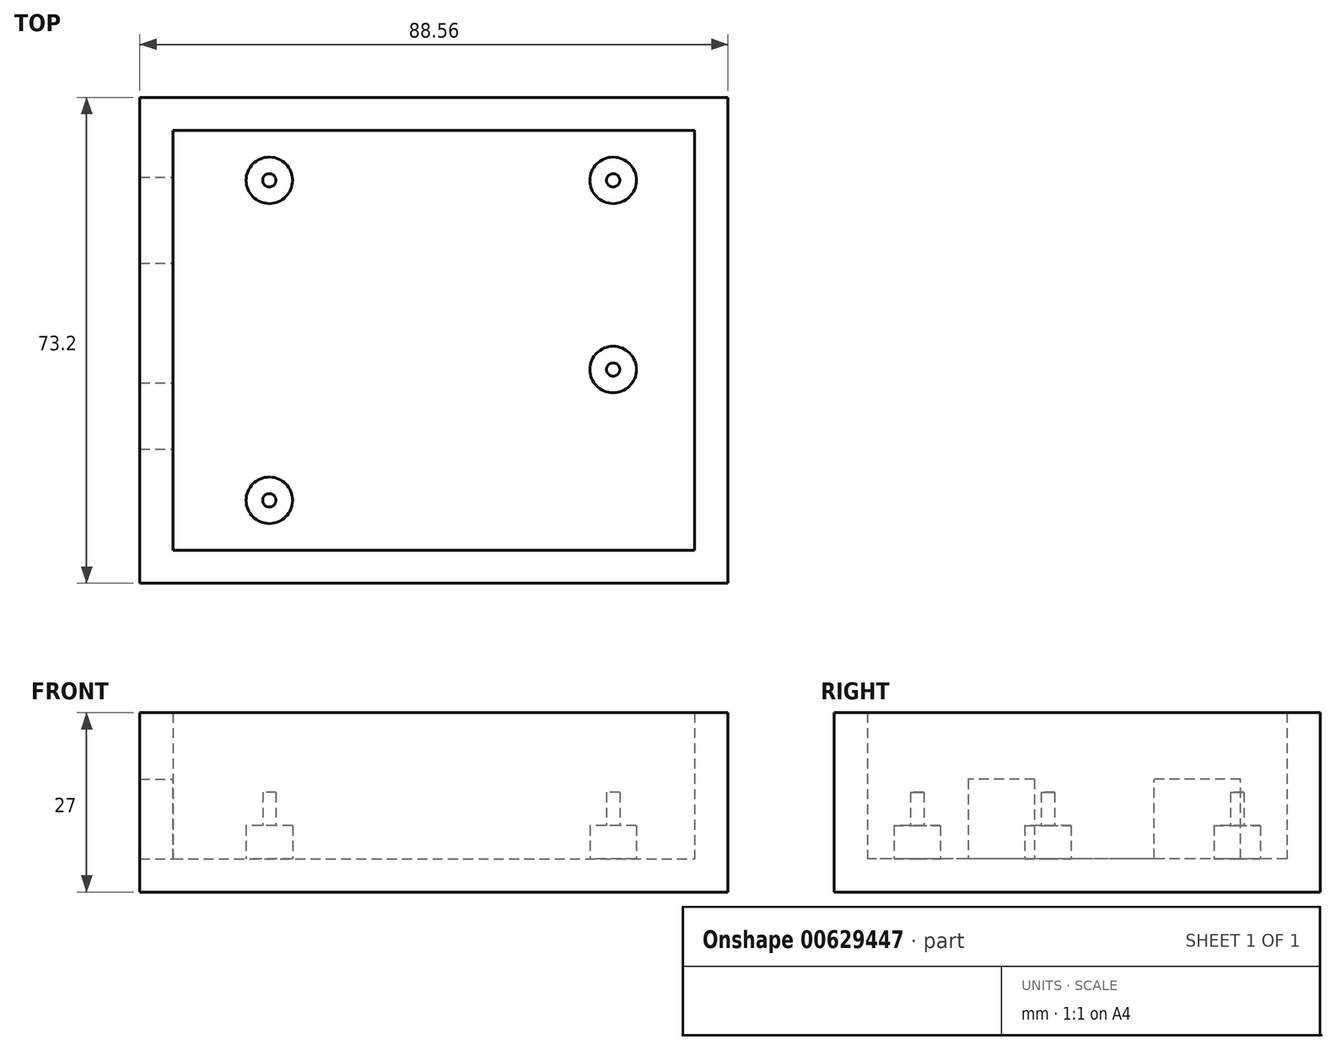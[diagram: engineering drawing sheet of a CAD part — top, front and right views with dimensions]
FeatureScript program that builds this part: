
annotation { "Feature Type Name" : "Feature", "Feature Type Description" : "" }
export const myFeature = defineFeature(function(context is Context, id is Id, definition is map)
    precondition{}
    {
        {
            var Q0;
            Q0=qCreatedBy(makeId("Top.planeOp"),FACE);
            var sketch = newSketch(context, id + "F0", { "sketchPlane" : qUnion([Q0])});
            skLineSegment(sketch, "E0.bottom", {"start": v(-32.7, 37.7) * mm, "end": v(33.07, 37.7) * mm});
            skLineSegment(sketch, "E0.top", {"start": v(-32.7, -15.5) * mm, "end": v(33.07, -15.5) * mm});
            skLineSegment(sketch, "E0.left", {"start": v(-32.7, 37.7) * mm, "end": v(-32.7, -15.5) * mm});
            skLineSegment(sketch, "E0.right", {"start": v(33.07, 37.7) * mm, "end": v(33.07, -15.5) * mm});
            skLineSegment(sketch, "E1.bottom", {"start": v(-39.2, 8.8) * mm, "end": v(-32.7, 8.8) * mm});
            skLineSegment(sketch, "E1.top", {"start": v(-39.2, -3.1) * mm, "end": v(-32.7, -3.1) * mm});
            skLineSegment(sketch, "E1.left", {"start": v(-39.2, 8.8) * mm, "end": v(-39.2, -3.1) * mm});
            skLineSegment(sketch, "E1.right", {"start": v(-32.7, 8.8) * mm, "end": v(-32.7, -3.1) * mm});
            skLineSegment(sketch, "E2.bottom", {"start": v(-36.41, 27.7) * mm, "end": v(-32.7, 27.7) * mm});
            skLineSegment(sketch, "E2.top", {"start": v(-36.41, 18.8) * mm, "end": v(-32.7, 18.8) * mm});
            skLineSegment(sketch, "E2.left", {"start": v(-36.41, 27.7) * mm, "end": v(-36.41, 18.8) * mm});
            skLineSegment(sketch, "E2.right", {"start": v(-32.7, 27.7) * mm, "end": v(-32.7, 18.8) * mm});
            skSolve(sketch);
        }
        {
            var Q0;
            Q0=qCreatedBy(makeId("Top.planeOp"),FACE);
            var sketch = newSketch(context, id + "F1", { "sketchPlane" : qUnion([Q0])});
            skLineSegment(sketch, "E3.bottom", {"start": v(-42.7, 47.7) * mm, "end": v(45.85, 47.7) * mm});
            skLineSegment(sketch, "E3.top", {"start": v(-42.7, -25.5) * mm, "end": v(45.85, -25.5) * mm});
            skLineSegment(sketch, "E3.left", {"start": v(-42.7, 47.7) * mm, "end": v(-42.7, -25.5) * mm});
            skLineSegment(sketch, "E3.right", {"start": v(45.85, 47.7) * mm, "end": v(45.85, -25.5) * mm});
            skLineSegment(sketch, "E4.direction1", {"start": v(-23.2, 35.2) * mm, "end": v(-23.2, -13) * mm, "construction": true});
            skSolve(sketch);
        }
        {
            var Q0;
            Q0=makeQuery(id+"F1.imprint","IMPRINT",FACE,{"disambiguationData":[TD([[makeQuery(id+"F1.imprint","IMPRINT",EDGE,{"derivedFrom":sQuery(id+"F1.wireOp",EDGE,"E3.bottom")}),-1.0]])]});
            extrude(context, id + "F2", {"entities" : qUnion([Q0]), "depth" : 22 * mm, "offsetDistance" : 25 * mm, "hasSecondDirection" : true, "secondDirectionOppositeDirection" : true, "secondDirectionDepth" : 5 * mm});
        }
        {
            var Q0;
            Q0=qCreatedBy(makeId("Top.planeOp"),FACE);
            var sketch = newSketch(context, id + "F3", { "sketchPlane" : qUnion([Q0])});
            skLineSegment(sketch, "E5.bottom", {"start": v(-37.7, 42.7) * mm, "end": v(40.85, 42.7) * mm});
            skLineSegment(sketch, "E5.top", {"start": v(-37.7, -20.5) * mm, "end": v(40.85, -20.5) * mm});
            skLineSegment(sketch, "E5.left", {"start": v(-37.7, 42.7) * mm, "end": v(-37.7, -20.5) * mm});
            skLineSegment(sketch, "E5.right", {"start": v(40.85, 42.7) * mm, "end": v(40.85, -20.5) * mm});
            skSolve(sketch);
        }
        {
            var Q0;
            Q0 = qSketchRegion(id + "F3", true);
            extrude(context, id + "F4", {"entities" : qUnion([Q0]), "operationType" : NewBodyOperationType.REMOVE, "depth" : 34.1 * mm, "offsetDistance" : 25 * mm});
        }
        {
            var Q0;
            Q0=qCreatedBy(makeId("Top.planeOp"),FACE);
            var sketch = newSketch(context, id + "F5", { "sketchPlane" : qUnion([Q0])});
            skLineSegment(sketch, "E6.bottom", {"start": v(-42.7, -25.5) * mm, "end": v(45.85, -25.5) * mm});
            skLineSegment(sketch, "E6.top", {"start": v(-42.7, 47.7) * mm, "end": v(45.85, 47.7) * mm});
            skLineSegment(sketch, "E6.left", {"start": v(-42.7, -25.5) * mm, "end": v(-42.7, 47.7) * mm});
            skLineSegment(sketch, "E6.right", {"start": v(45.85, -25.5) * mm, "end": v(45.85, 47.7) * mm});
            skSolve(sketch);
        }
        {
            var Q0;
            Q0=makeQuery(id+"F4.boolean.opBoolean","COPY",FACE,{"derivedFrom":makeQuery(id+"F4.opExtrude","SWEPT_FACE",FACE,{"disambiguationData":[OSD([sQuery(id+"F3.wireOp",EDGE,"E5.left")])]})});
            var sketch = newSketch(context, id + "F6", { "sketchPlane" : qUnion([Q0])});
            skLineSegment(sketch, "E7.bottom", {"start": v(35.7, 0) * mm, "end": v(22.7, 0) * mm});
            skLineSegment(sketch, "E7.top", {"start": v(35.7, 12) * mm, "end": v(22.7, 12) * mm});
            skLineSegment(sketch, "E7.left", {"start": v(35.7, 0) * mm, "end": v(35.7, 12) * mm});
            skLineSegment(sketch, "E7.right", {"start": v(22.7, 0) * mm, "end": v(22.7, 12) * mm});
            skLineSegment(sketch, "E8.bottom", {"start": v(4.7, 12) * mm, "end": v(-5.3, 12) * mm});
            skLineSegment(sketch, "E8.top", {"start": v(4.7, 0) * mm, "end": v(-5.3, 0) * mm});
            skLineSegment(sketch, "E8.left", {"start": v(4.7, 12) * mm, "end": v(4.7, 0) * mm});
            skLineSegment(sketch, "E8.right", {"start": v(-5.3, 12) * mm, "end": v(-5.3, 0) * mm});
            skSolve(sketch);
        }
        {
            var Q0;
            Q0=makeQuery(id+"F5.imprint","IMPRINT",FACE,{"disambiguationData":[TD([[makeQuery(id+"F5.imprint","IMPRINT",EDGE,{"derivedFrom":sQuery(id+"F5.wireOp",EDGE,"E6.bottom")}),1.0]])]});
            var sketch = newSketch(context, id + "F7", { "sketchPlane" : qUnion([Q0])});
            skCircle(sketch, "E9.0", {"center": v(28.57, 35.2) * mm, "radius": 3.5 * mm});
            skCircle(sketch, "E9.1", {"center": v(28.57, 6.7) * mm, "radius": 3.5 * mm});
            skCircle(sketch, "E9.2", {"center": v(-23.2, 35.2) * mm, "radius": 3.5 * mm});
            skCircle(sketch, "E9.3", {"center": v(-23.2, -13) * mm, "radius": 3.5 * mm});
            skCircle(sketch, "E10", {"center": v(28.57, 35.2) * mm, "radius": 1 * mm});
            skCircle(sketch, "E11", {"center": v(28.57, 6.7) * mm, "radius": 1 * mm});
            skCircle(sketch, "E12", {"center": v(-23.2, 35.2) * mm, "radius": 1 * mm});
            skCircle(sketch, "E13", {"center": v(-23.2, -13) * mm, "radius": 1 * mm});
            skSolve(sketch);
        }
        {
            var Q0;
            Q0 = qSketchRegion(id + "F7", true);
            extrude(context, id + "F8", {"entities" : qUnion([Q0]), "operationType" : NewBodyOperationType.ADD, "depth" : 5 * mm, "offsetDistance" : 25 * mm});
        }
        {
            var Q0;
            Q0 = qSketchRegion(id + "F6", true);
            extrude(context, id + "F9", {"entities" : qUnion([Q0]), "operationType" : NewBodyOperationType.REMOVE, "oppositeDirection" : true, "depth" : 25 * mm, "offsetDistance" : 25 * mm});
        }
        {
            var Q0;
            Q0=makeQuery(id+"F7.imprint","IMPRINT",FACE,{"disambiguationData":[TD([[makeQuery(id+"F7.imprint","IMPRINT",EDGE,{"derivedFrom":sQuery(id+"F7.wireOp",EDGE,"E10")}),1.0]])]});
            var sketch = newSketch(context, id + "F10", { "sketchPlane" : qUnion([Q0])});
            skCircle(sketch, "E14.0", {"center": v(28.57, 35.2) * mm, "radius": 1 * mm});
            skCircle(sketch, "E14.1", {"center": v(28.57, 6.7) * mm, "radius": 1 * mm});
            skCircle(sketch, "E14.2", {"center": v(-23.2, -13) * mm, "radius": 1 * mm});
            skCircle(sketch, "E14.3", {"center": v(-23.2, 35.2) * mm, "radius": 1 * mm});
            skSolve(sketch);
        }
        {
            var Q0;
            Q0 = qSketchRegion(id + "F10", true);
            extrude(context, id + "F11", {"entities" : qUnion([Q0]), "operationType" : NewBodyOperationType.ADD, "depth" : 10 * mm, "offsetDistance" : 25 * mm});
        }
    });
